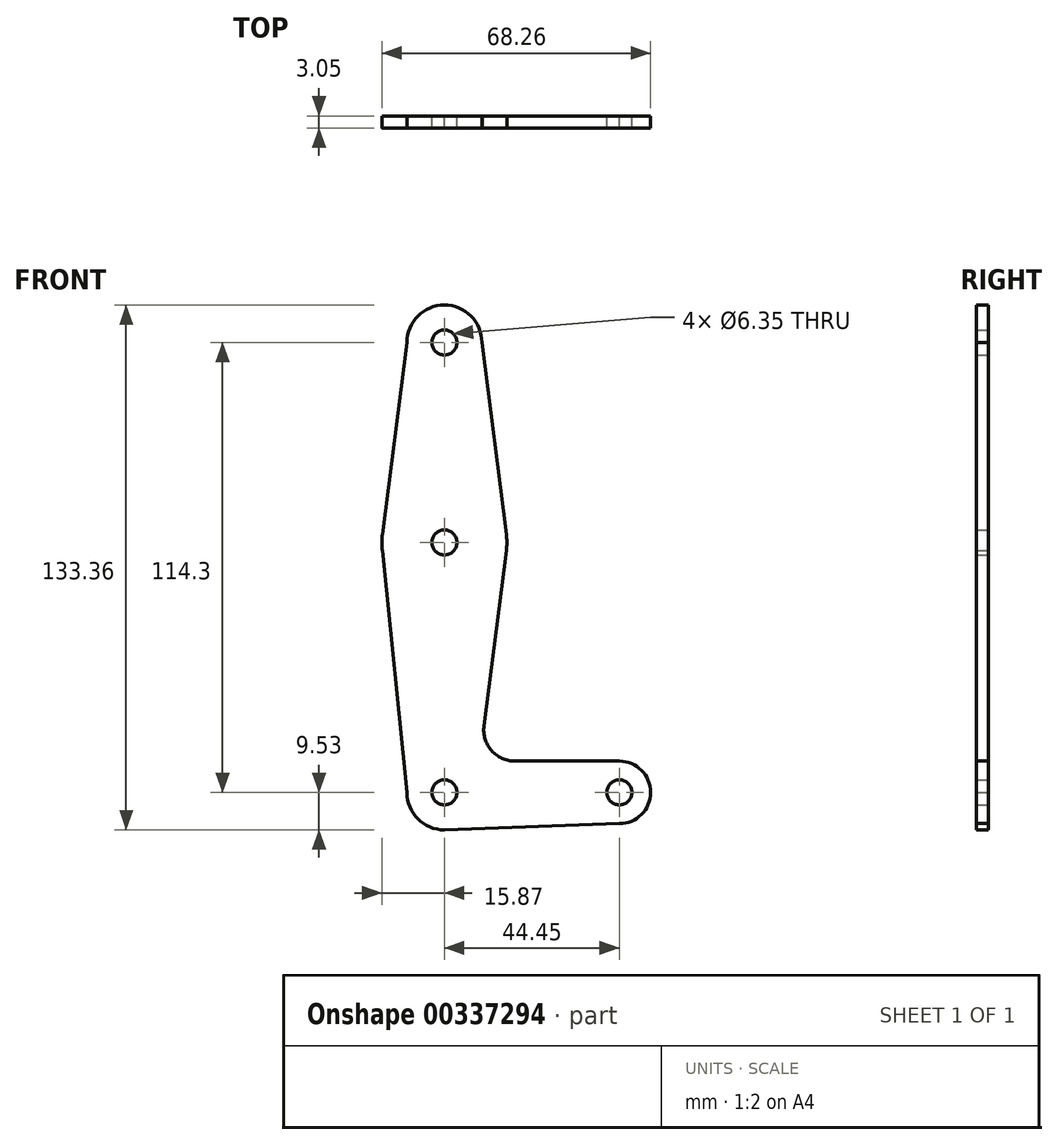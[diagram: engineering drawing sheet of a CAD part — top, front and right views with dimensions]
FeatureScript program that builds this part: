
annotation { "Feature Type Name" : "Feature", "Feature Type Description" : "" }
export const myFeature = defineFeature(function(context is Context, id is Id, definition is map)
    precondition{}
    {
        {
            var Q0;
            Q0=qCreatedBy(makeId("Front.planeOp"),FACE);
            var sketch = newSketch(context, id + "F0", { "sketchPlane" : qUnion([Q0])});
            skLineSegment(sketch, "E0", {"start": v(0, 0) * mm, "end": v(0, 114.3) * mm});
            skLineSegment(sketch, "E1", {"start": v(0, 0) * mm, "end": v(44.45, 0) * mm});
            skCircle(sketch, "E2", {"center": v(0, 114.3) * mm, "radius": 9.53 * mm});
            skCircle(sketch, "E3", {"center": v(0, 0) * mm, "radius": 9.53 * mm});
            skCircle(sketch, "E4", {"center": v(44.45, 0) * mm, "radius": 7.94 * mm});
            skCircle(sketch, "E5", {"center": v(0, 63.5) * mm, "radius": 15.88 * mm});
            skLineSegment(sketch, "E6", {"start": v(-9.53, 114.3) * mm, "end": v(-15.75, 65.5) * mm});
            skLineSegment(sketch, "E7", {"start": v(-9.53, 0) * mm, "end": v(-15.75, 61.5) * mm});
            skLineSegment(sketch, "E8", {"start": v(9.53, 114.3) * mm, "end": v(15.75, 65.5) * mm});
            skLineSegment(sketch, "E9", {"start": v(10.06, 16.9) * mm, "end": v(15.75, 61.5) * mm});
            skLineSegment(sketch, "E10", {"start": v(17.95, 7.94) * mm, "end": v(44.45, 7.94) * mm});
            skLineSegment(sketch, "E11", {"start": v(0, -9.52) * mm, "end": v(44.45, -7.94) * mm});
            skCircle(sketch, "E12", {"center": v(0, 114.3) * mm, "radius": 3.18 * mm});
            skCircle(sketch, "E13", {"center": v(0, 63.5) * mm, "radius": 3.18 * mm});
            skCircle(sketch, "E14", {"center": v(0, 0) * mm, "radius": 3.18 * mm});
            skCircle(sketch, "E15", {"center": v(44.45, 0) * mm, "radius": 3.18 * mm});
            skArc(sketch, "E16.filletArc", {"start": v(10.06, 16.9) * mm, "mid": v(11.98, 10.63) * mm, "end": v(17.95, 7.94) * mm});
            skSolve(sketch);
        }
        {
            var Q0;
            {var subQ5=sQuery(id+"F0.wireOp",EDGE,"E6");Q0=makeQuery(id+"F0.imprint","IMPRINT",FACE,{"disambiguationData":[TD([[makeQuery(id+"F0.imprint","IMPRINT",EDGE,{"derivedFrom":subQ5}),1.0]])]});}
            var Q1;
            {var subQ5=sQuery(id+"F0.wireOp",EDGE,"E8");Q1=makeQuery(id+"F0.imprint","IMPRINT",FACE,{"disambiguationData":[TD([[makeQuery(id+"F0.imprint","IMPRINT",EDGE,{"derivedFrom":subQ5}),-1.0]])]});}
            var Q2;
            Q2=makeQuery(id+"F0.imprint","IMPRINT",FACE,{"disambiguationData":[TD([[makeQuery(id+"F0.imprint","IMPRINT",EDGE,{"derivedFrom":sQuery(id+"F0.wireOp",EDGE,"E12")}),-1.0]])]});
            var Q3;
            {var subQ0=sQuery(id+"F0.wireOp",EDGE,"E5");var subQ2=sQuery(id+"F0.wireOp",EDGE,"E0");var subQ7=makeQuery(id+"F0.imprint","INTERSECT",VERTEX,{"disambiguationData":[OD(0.0)],"derivedFrom":[subQ2,subQ0]});Q3=makeQuery(id+"F0.imprint","IMPRINT",FACE,{"disambiguationData":[TD([[makeQuery(id+"F0.imprint","IMPRINT",EDGE,{"disambiguationData":[TD([[subQ7,-1.0]])],"derivedFrom":subQ2}),1.0]])]});}
            var Q4;
            {var subQ5=sQuery(id+"F0.wireOp",EDGE,"E7");Q4=makeQuery(id+"F0.imprint","IMPRINT",FACE,{"disambiguationData":[TD([[makeQuery(id+"F0.imprint","IMPRINT",EDGE,{"derivedFrom":subQ5}),-1.0]])]});}
            var Q5;
            {var subQ10=sQuery(id+"F0.wireOp",EDGE,"E9");Q5=makeQuery(id+"F0.imprint","IMPRINT",FACE,{"disambiguationData":[TD([[makeQuery(id+"F0.imprint","IMPRINT",EDGE,{"derivedFrom":subQ10}),1.0]])]});}
            var Q6;
            {var subQ4=sQuery(id+"F0.wireOp",EDGE,"E0");var subQ6=sQuery(id+"F0.wireOp",EDGE,"E14");var subQ10=makeQuery(id+"F0.imprint","INTERSECT",VERTEX,{"derivedFrom":[subQ4,subQ6]});Q6=makeQuery(id+"F0.imprint","IMPRINT",FACE,{"disambiguationData":[TD([[makeQuery(id+"F0.imprint","IMPRINT",EDGE,{"disambiguationData":[TD([[subQ10,-1.0]])],"derivedFrom":subQ4}),1.0]])]});}
            var Q7;
            {var subQ0=sQuery(id+"F0.wireOp",EDGE,"E14");var subQ1=sQuery(id+"F0.wireOp",EDGE,"E0");var subQ2=makeQuery(id+"F0.imprint","INTERSECT",VERTEX,{"derivedFrom":[subQ1,subQ0]});Q7=makeQuery(id+"F0.imprint","IMPRINT",FACE,{"disambiguationData":[TD([[makeQuery(id+"F0.imprint","IMPRINT",EDGE,{"disambiguationData":[TD([[subQ2,-1.0]])],"derivedFrom":subQ1}),-1.0]])]});}
            var Q8;
            {var subQ0=sQuery(id+"F0.wireOp",EDGE,"E4");var subQ1=sQuery(id+"F0.wireOp",EDGE,"E1");var subQ2=makeQuery(id+"F0.imprint","INTERSECT",VERTEX,{"derivedFrom":[subQ1,subQ0]});Q8=makeQuery(id+"F0.imprint","IMPRINT",FACE,{"disambiguationData":[TD([[makeQuery(id+"F0.imprint","IMPRINT",EDGE,{"disambiguationData":[TD([[subQ2,1.0]])],"derivedFrom":subQ1}),-1.0]])]});}
            var Q9;
            Q9=makeQuery(id+"F0.imprint","IMPRINT",FACE,{"disambiguationData":[TD([[makeQuery(id+"F0.imprint","IMPRINT",EDGE,{"derivedFrom":sQuery(id+"F0.wireOp",EDGE,"E15")}),-1.0]])]});
            var Q10;
            {var subQ0=sQuery(id+"F0.wireOp",EDGE,"E5");var subQ2=sQuery(id+"F0.wireOp",EDGE,"E0");var subQ5=makeQuery(id+"F0.imprint","INTERSECT",VERTEX,{"disambiguationData":[OD(0.0)],"derivedFrom":[subQ2,subQ0]});Q10=makeQuery(id+"F0.imprint","IMPRINT",FACE,{"disambiguationData":[TD([[makeQuery(id+"F0.imprint","IMPRINT",EDGE,{"disambiguationData":[TD([[subQ5,-1.0]])],"derivedFrom":subQ2}),-1.0]])]});}
            extrude(context, id + "F1", {"entities" : qUnion([Q0, Q1, Q2, Q3, Q4, Q5, Q6, Q7, Q8, Q9, Q10]), "depth" : 3.05 * mm});
        }
    });
